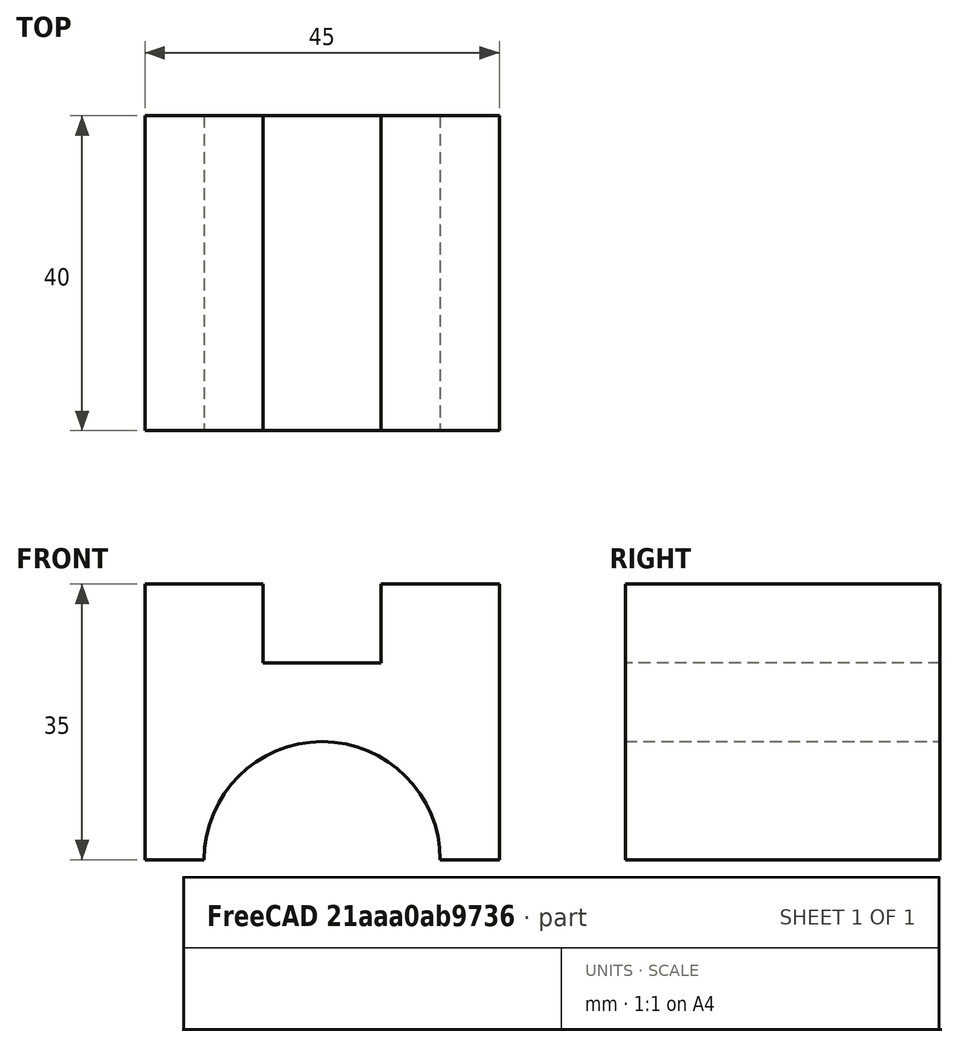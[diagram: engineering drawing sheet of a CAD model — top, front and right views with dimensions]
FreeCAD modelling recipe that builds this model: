
FCSTD DOCUMENT  (FreeCAD 0.19R24291 (Git))
Label: iso_prac2
License: All rights reserved
LicenseURL: http://en.wikipedia.org/wiki/All_rights_reserved
objects: Sketcher::SketchObject×1, PartDesign::Pad×1, PartDesign::Body×1
note: 4 computed .brp shape members not serialized (recipe doc carries the construction recipe); baked Part::Feature solids carry a one-line shape summary decoded from their .brp

FEATURE [Sketcher::SketchObject] Sketch
  FullyConstrained = true
  MapMode = 5
  Placement = pos=(0,0,0) rot=(1,0,0;1.5708rad)
  Support = -> [XZ_Plane]
  sketch-geometry (10):
    g0: LineSegment StartX=-22.5 StartY=-8.13178e-08 StartZ=0 EndX=-22.5 EndY=35 EndZ=0
    g1: LineSegment StartX=-22.5 StartY=35 StartZ=0 EndX=-7.5 EndY=35 EndZ=0
    g2: LineSegment StartX=-7.5 StartY=35 StartZ=0 EndX=-7.5 EndY=25 EndZ=0
    g3: LineSegment StartX=-7.5 StartY=25 StartZ=0 EndX=7.5 EndY=25 EndZ=0
    g4: LineSegment StartX=7.5 StartY=25 StartZ=0 EndX=7.5 EndY=35 EndZ=0
    g5: LineSegment StartX=7.5 StartY=35 StartZ=0 EndX=22.5 EndY=35 EndZ=0
    g6: LineSegment StartX=22.5 StartY=35 StartZ=0 EndX=22.5 EndY=-8.13178e-08 EndZ=0
    g7: LineSegment StartX=22.5 StartY=-8.13178e-08 StartZ=0 EndX=15 EndY=-8.13178e-08 EndZ=0
    g8: ArcOfCircle CenterX=0 CenterY=0 CenterZ=0 NormalX=0 NormalY=0 NormalZ=1 AngleXU=0 Radius=15 StartAngle=6.28319 EndAngle=9.42478
    g9: LineSegment StartX=-15 StartY=-8.13178e-08 StartZ=0 EndX=-22.5 EndY=-8.13178e-08 EndZ=0
  constraints (30):
    c: Vertical(g0)
    c: Coincident(g0,g1)
    c: Horizontal(g1)
    c: Coincident(g1,g2)
    c: Vertical(g2)
    c: Coincident(g2,g3)
    c: Horizontal(g3)
    c: Coincident(g3,g4)
    c: Coincident(g4,g5)
    c: Horizontal(g5)
    c: Coincident(g5,g6)
    c: Vertical(g6)
    c: Coincident(g6,g7)
    c: Horizontal(g7)
    c: Coincident(g8,g9)
    c: Coincident(g9,g0)
    c: Horizontal(g9)
    c: Vertical(g4)
    c: Equal(g1,g5)
    c: Equal(g1,g3)
    c: Equal(g9,g7)
    c: DistanceX(g1,g1) = 15
    c: Equal(g6,g0)
    c: DistanceY(g0,g0) = 35
    c: Equal(g2,g4)
    c: DistanceY(g4,g4) = 10
    c: Coincident(g8,g7)
    c: Radius(g8) = 15
    c: Coincident(g8,g-1)
    c: DistanceX(g9,g9) = 7.5
FEATURE [PartDesign::Pad] Pad
  Direction = (1,1,1)
  Length = 40
  Length2 = 100
  Placement = pos=(0,0,0) rot=(1,0,0;1.5708rad)
  Profile = -> Sketch
  Refine = true
  Type = 0
FEATURE [PartDesign::Body] Body
  Group = -> [Sketch,Pad]
  Origin = -> Origin
  Tip = -> Pad
